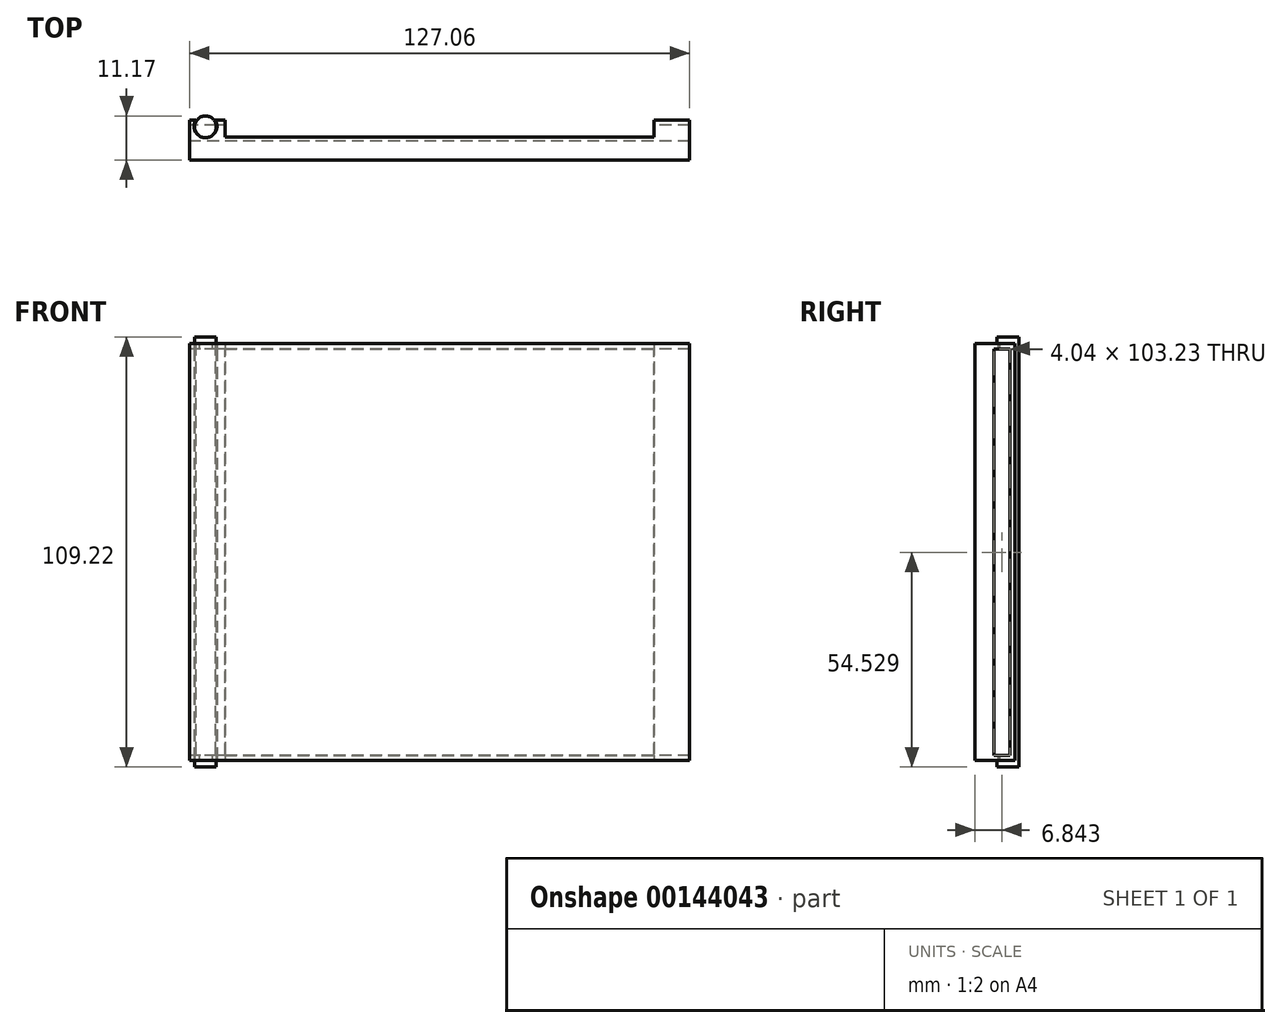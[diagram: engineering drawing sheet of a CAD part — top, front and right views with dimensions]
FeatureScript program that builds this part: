
annotation { "Feature Type Name" : "Feature", "Feature Type Description" : "" }
export const myFeature = defineFeature(function(context is Context, id is Id, definition is map)
    precondition{}
    {
        {
            var Q0;
            Q0=qCreatedBy(makeId("Front.planeOp"),FACE);
            var sketch = newSketch(context, id + "F0", { "sketchPlane" : qUnion([Q0])});
            skLineSegment(sketch, "E0.bottom", {"start": v(63.53, -52.94) * mm, "end": v(-63.53, -52.94) * mm});
            skLineSegment(sketch, "E0.top", {"start": v(63.53, 52.94) * mm, "end": v(-63.53, 52.94) * mm});
            skLineSegment(sketch, "E0.left", {"start": v(63.53, -52.94) * mm, "end": v(63.53, 52.94) * mm});
            skLineSegment(sketch, "E0.right", {"start": v(-63.53, -52.94) * mm, "end": v(-63.53, 52.94) * mm});
            skPoint(sketch, "E0.middle", {"position": v(0, 0) * mm});
            skSolve(sketch);
        }
        {
            var Q0;
            Q0=qSketchRegion(id+"F0",true);
            extrude(context, id + "F1", {"entities" : qUnion([Q0]), "depth" : 10.16 * mm});
        }
        {
            var Q0;
            Q0=qCreatedBy(makeId("Front.planeOp"),FACE);
            var sketch = newSketch(context, id + "F2", { "sketchPlane" : qUnion([Q0])});
            skLineSegment(sketch, "E1.bottom", {"start": v(-54.5, 52.94) * mm, "end": v(54.5, 52.94) * mm});
            skLineSegment(sketch, "E1.top", {"start": v(-54.5, -52.94) * mm, "end": v(54.5, -52.94) * mm});
            skLineSegment(sketch, "E1.left", {"start": v(-54.5, 52.94) * mm, "end": v(-54.5, -52.94) * mm});
            skLineSegment(sketch, "E1.right", {"start": v(54.5, 52.94) * mm, "end": v(54.5, -52.94) * mm});
            skPoint(sketch, "E1.middle", {"position": v(0, 0) * mm});
            skSolve(sketch);
        }
        {
            var Q0;
            Q0=makeQuery(id+"F2.imprint","IMPRINT",FACE,{"disambiguationData":[TD([[makeQuery(id+"F2.imprint","IMPRINT",EDGE,{"derivedFrom":sQuery(id+"F2.wireOp",EDGE,"E1.bottom")}),-1.0]])]});
            extrude(context, id + "F3", {"entities" : qUnion([Q0]), "operationType" : NewBodyOperationType.REMOVE, "depth" : 4.32 * mm});
        }
        {
            var Q0;
            Q0=qCreatedBy(makeId("Top.planeOp"),FACE);
            var sketch = newSketch(context, id + "F4", { "sketchPlane" : qUnion([Q0])});
            skCircle(sketch, "E2", {"center": v(-59.48, -1.57) * mm, "radius": 2.91 * mm});
            skSolve(sketch);
        }
        {
            var Q0;
            Q0=qSketchRegion(id+"F4",true);
            extrude(context, id + "F5", {"entities" : qUnion([Q0]), "operationType" : NewBodyOperationType.REMOVE, "depth" : 62.1 * mm, "hasSecondDirection" : true, "secondDirectionOppositeDirection" : true, "secondDirectionDepth" : 60.44 * mm});
        }
        {
            var Q0;
            Q0=qCreatedBy(makeId("Top.planeOp"),FACE);
            var sketch = newSketch(context, id + "F6", { "sketchPlane" : qUnion([Q0])});
            skCircle(sketch, "E3", {"center": v(-59.48, -1.75) * mm, "radius": 2.76 * mm});
            skSolve(sketch);
        }
        {
            var Q0;
            Q0=qSketchRegion(id+"F6",true);
            extrude(context, id + "F7", {"entities" : qUnion([Q0]), "operationType" : NewBodyOperationType.ADD, "depth" : 54.6 * mm, "hasSecondDirection" : true, "secondDirectionOppositeDirection" : true, "secondDirectionDepth" : 54.6 * mm});
        }
        {
            var Q0;
            Q0=qCreatedBy(makeId("Right.planeOp"),FACE);
            var sketch = newSketch(context, id + "F8", { "sketchPlane" : qUnion([Q0])});
            skLineSegment(sketch, "E4.bottom", {"start": v(-1.3, 51.53) * mm, "end": v(-5.34, 51.53) * mm});
            skLineSegment(sketch, "E4.top", {"start": v(-1.3, -51.7) * mm, "end": v(-5.34, -51.7) * mm});
            skLineSegment(sketch, "E4.left", {"start": v(-1.3, 51.53) * mm, "end": v(-1.3, -51.7) * mm});
            skLineSegment(sketch, "E4.right", {"start": v(-5.34, 51.53) * mm, "end": v(-5.34, -51.7) * mm});
            skSolve(sketch);
        }
        {
            var Q0;
            Q0=qSketchRegion(id+"F8",true);
            extrude(context, id + "F9", {"entities" : qUnion([Q0]), "operationType" : NewBodyOperationType.REMOVE, "depth" : 79 * mm, "hasSecondDirection" : true, "secondDirectionOppositeDirection" : true, "secondDirectionDepth" : 74.9 * mm});
        }
        {
            var Q0;
            Q0=qCreatedBy(makeId("Right.planeOp"),FACE);
            var sketch = newSketch(context, id + "F10", { "sketchPlane" : qUnion([Q0])});
            skLineSegment(sketch, "E5.bottom", {"start": v(-3.31, 51.47) * mm, "end": v(-4.6, 51.47) * mm});
            skLineSegment(sketch, "E5.top", {"start": v(-3.31, -50.55) * mm, "end": v(-4.6, -50.55) * mm});
            skLineSegment(sketch, "E5.left", {"start": v(-3.31, 51.47) * mm, "end": v(-3.31, -50.55) * mm});
            skLineSegment(sketch, "E5.right", {"start": v(-4.6, 51.47) * mm, "end": v(-4.6, -50.55) * mm});
            skSolve(sketch);
        }
        {
            var Q0;
            Q0=qSketchRegion(id+"F10",true);
            extrude(context, id + "F11", {"entities" : qUnion([Q0]), "operationType" : NewBodyOperationType.REMOVE, "depth" : 76.04 * mm, "hasSecondDirection" : true, "secondDirectionOppositeDirection" : true, "secondDirectionDepth" : 72.7 * mm});
        }
    });
